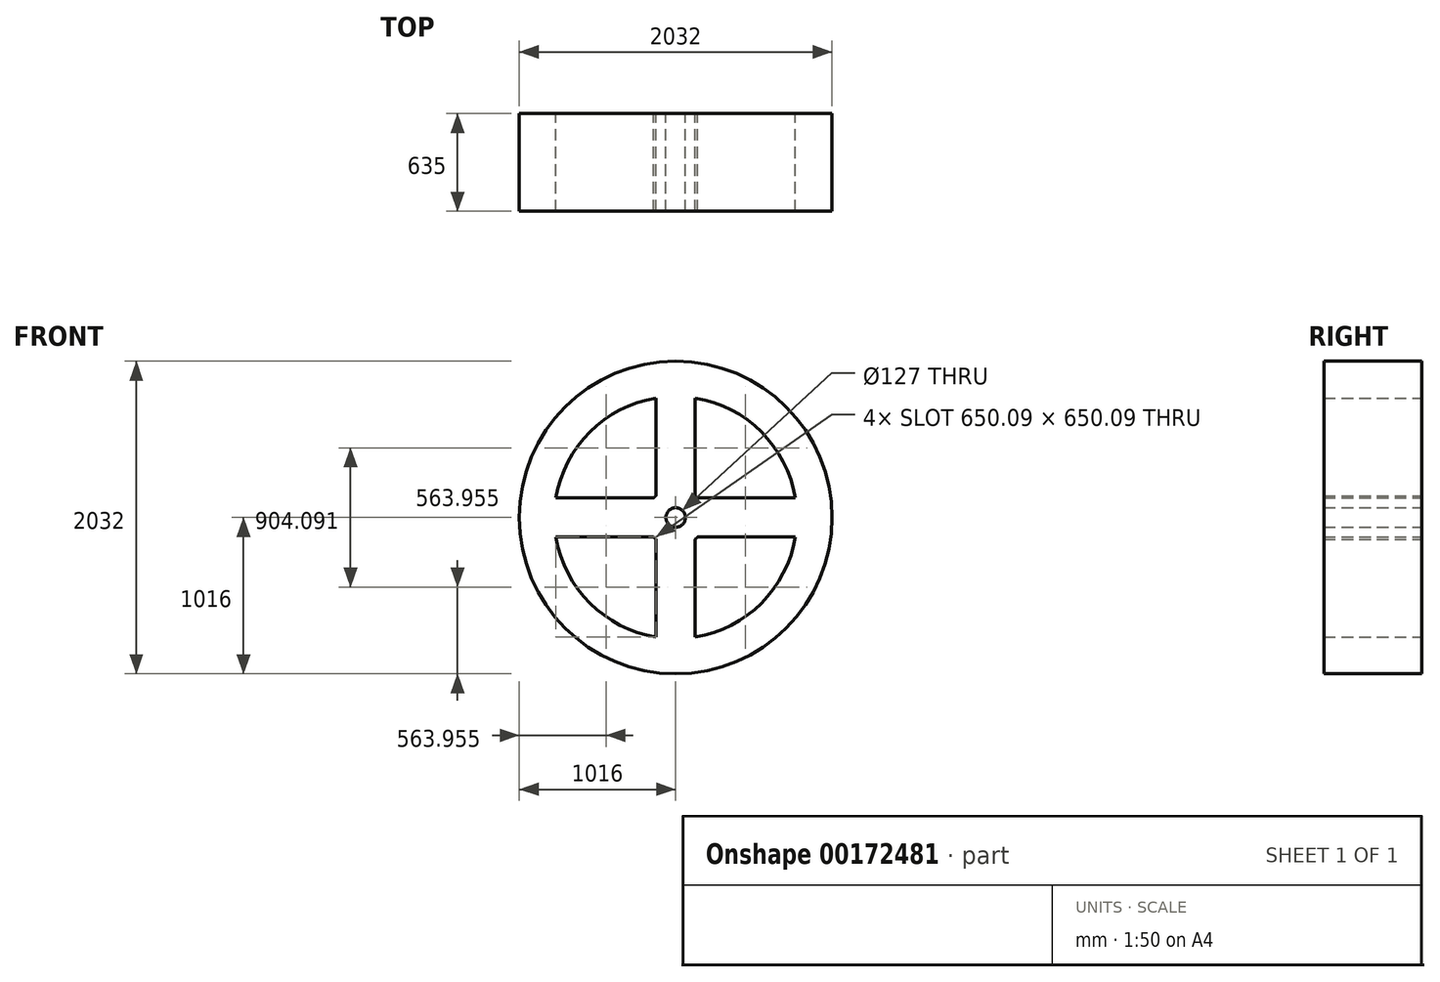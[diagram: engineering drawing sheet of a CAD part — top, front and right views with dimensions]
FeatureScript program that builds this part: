
annotation { "Feature Type Name" : "Feature", "Feature Type Description" : "" }
export const myFeature = defineFeature(function(context is Context, id is Id, definition is map)
    precondition{}
    {
        {
            var Q0;
            Q0=qCreatedBy(makeId("Front.planeOp"),FACE);
            var sketch = newSketch(context, id + "F0", { "sketchPlane" : qUnion([Q0])});
            skCircle(sketch, "E0", {"center": v(0, 0) * mm, "radius": 1016 * mm});
            skArc(sketch, "E1", {"start": v(142, 127) * mm, "mid": v(134.7, 134.7) * mm, "end": v(127, 142) * mm});
            skArc(sketch, "E2", {"start": v(777.1, 127) * mm, "mid": v(556.78, 556.78) * mm, "end": v(127, 777.1) * mm});
            skLineSegment(sketch, "E3", {"start": v(0, 0) * mm, "end": v(0, 1016) * mm});
            skLineSegment(sketch, "E4.MirrorCS", {"start": v(-127, 142) * mm, "end": v(-127, 777.1) * mm});
            skLineSegment(sketch, "E5", {"start": v(0, 0) * mm, "end": v(0, -1016) * mm});
            skLineSegment(sketch, "E6", {"start": v(0, 0) * mm, "end": v(1016, 0) * mm});
            skLineSegment(sketch, "E7", {"start": v(0, 0) * mm, "end": v(-1016, 0) * mm});
            skLineSegment(sketch, "E8.0", {"start": v(-127, -142) * mm, "end": v(-127, -777.1) * mm});
            skLineSegment(sketch, "E9.0", {"start": v(127, -142) * mm, "end": v(127, -777.1) * mm});
            skLineSegment(sketch, "E10.0", {"start": v(-142, -127) * mm, "end": v(-777.1, -127) * mm});
            skLineSegment(sketch, "E11.0", {"start": v(-142, 127) * mm, "end": v(-777.1, 127) * mm});
            skLineSegment(sketch, "E12.0", {"start": v(142, -127) * mm, "end": v(777.1, -127) * mm});
            skCircle(sketch, "E13", {"center": v(0, 0) * mm, "radius": 63.5 * mm});
            skLineSegment(sketch, "E14.trimOffspring", {"start": v(1008.03, -127) * mm, "end": v(1016, -127) * mm});
            skLineSegment(sketch, "E15.trimOffspring", {"start": v(1008.03, 127) * mm, "end": v(1016, 127) * mm});
            skLineSegment(sketch, "E16.trimOffspring", {"start": v(127, 1008.03) * mm, "end": v(127, 1016) * mm});
            skLineSegment(sketch, "E17.trimOffspring", {"start": v(-127, 1008.03) * mm, "end": v(-127, 1016) * mm});
            skLineSegment(sketch, "E18.trimOffspring", {"start": v(-1008.03, 127) * mm, "end": v(-1016, 127) * mm});
            skLineSegment(sketch, "E19.trimOffspring", {"start": v(-1008.03, -127) * mm, "end": v(-1016, -127) * mm});
            skLineSegment(sketch, "E20.trimOffspring", {"start": v(-127, -1008.03) * mm, "end": v(-127, -1016) * mm});
            skLineSegment(sketch, "E21.trimOffspring", {"start": v(127, -1008.03) * mm, "end": v(127, -1016) * mm});
            skArc(sketch, "E22.trimOffspring", {"start": v(-127, 142) * mm, "mid": v(-134.7, 134.7) * mm, "end": v(-142, 127) * mm});
            skArc(sketch, "E23.trimOffspring", {"start": v(-142, -127) * mm, "mid": v(-134.7, -134.7) * mm, "end": v(-127, -142) * mm});
            skArc(sketch, "E24.trimOffspring", {"start": v(127, -142) * mm, "mid": v(134.7, -134.7) * mm, "end": v(142, -127) * mm});
            skLineSegment(sketch, "E25.trimOffspring", {"start": v(127, 142) * mm, "end": v(127, 777.1) * mm});
            skLineSegment(sketch, "E26.trimOffspring", {"start": v(142, 127) * mm, "end": v(777.1, 127) * mm});
            skPoint(sketch, "E27.0.start.orphan", {"position": v(127, 0) * mm});
            skPoint(sketch, "E28.orphan", {"position": v(-127, 0) * mm});
            skArc(sketch, "E29.trimOffspring", {"start": v(127, -777.1) * mm, "mid": v(556.78, -556.78) * mm, "end": v(777.1, -127) * mm});
            skArc(sketch, "E30.trimOffspring", {"start": v(-777.1, -127) * mm, "mid": v(-556.78, -556.78) * mm, "end": v(-127, -777.1) * mm});
            skArc(sketch, "E31.trimOffspring", {"start": v(-127, 777.1) * mm, "mid": v(-556.78, 556.78) * mm, "end": v(-777.1, 127) * mm});
            skSolve(sketch);
        }
        {
            var Q0;
            Q0=makeQuery(id+"F0.imprint","IMPRINT",FACE,{"disambiguationData":[TD([[makeQuery(id+"F0.imprint","IMPRINT",EDGE,{"derivedFrom":sQuery(id+"F0.wireOp",EDGE,"E8.0")}),1.0]])]});
            var Q1;
            Q1=makeQuery(id+"F0.imprint","IMPRINT",FACE,{"disambiguationData":[TD([[makeQuery(id+"F0.imprint","IMPRINT",EDGE,{"derivedFrom":sQuery(id+"F0.wireOp",EDGE,"E9.0")}),-1.0]])]});
            var Q2;
            Q2=makeQuery(id+"F0.imprint","IMPRINT",FACE,{"disambiguationData":[TD([[makeQuery(id+"F0.imprint","IMPRINT",EDGE,{"derivedFrom":sQuery(id+"F0.wireOp",EDGE,"E4.MirrorCS")}),-1.0]])]});
            var Q3;
            Q3=makeQuery(id+"F0.imprint","IMPRINT",FACE,{"disambiguationData":[TD([[makeQuery(id+"F0.imprint","IMPRINT",EDGE,{"derivedFrom":sQuery(id+"F0.wireOp",EDGE,"E1")}),1.0]])]});
            extrude(context, id + "F1", {"entities" : qUnion([Q0, Q1, Q2, Q3]), "depth" : 635 * mm});
        }
    });
